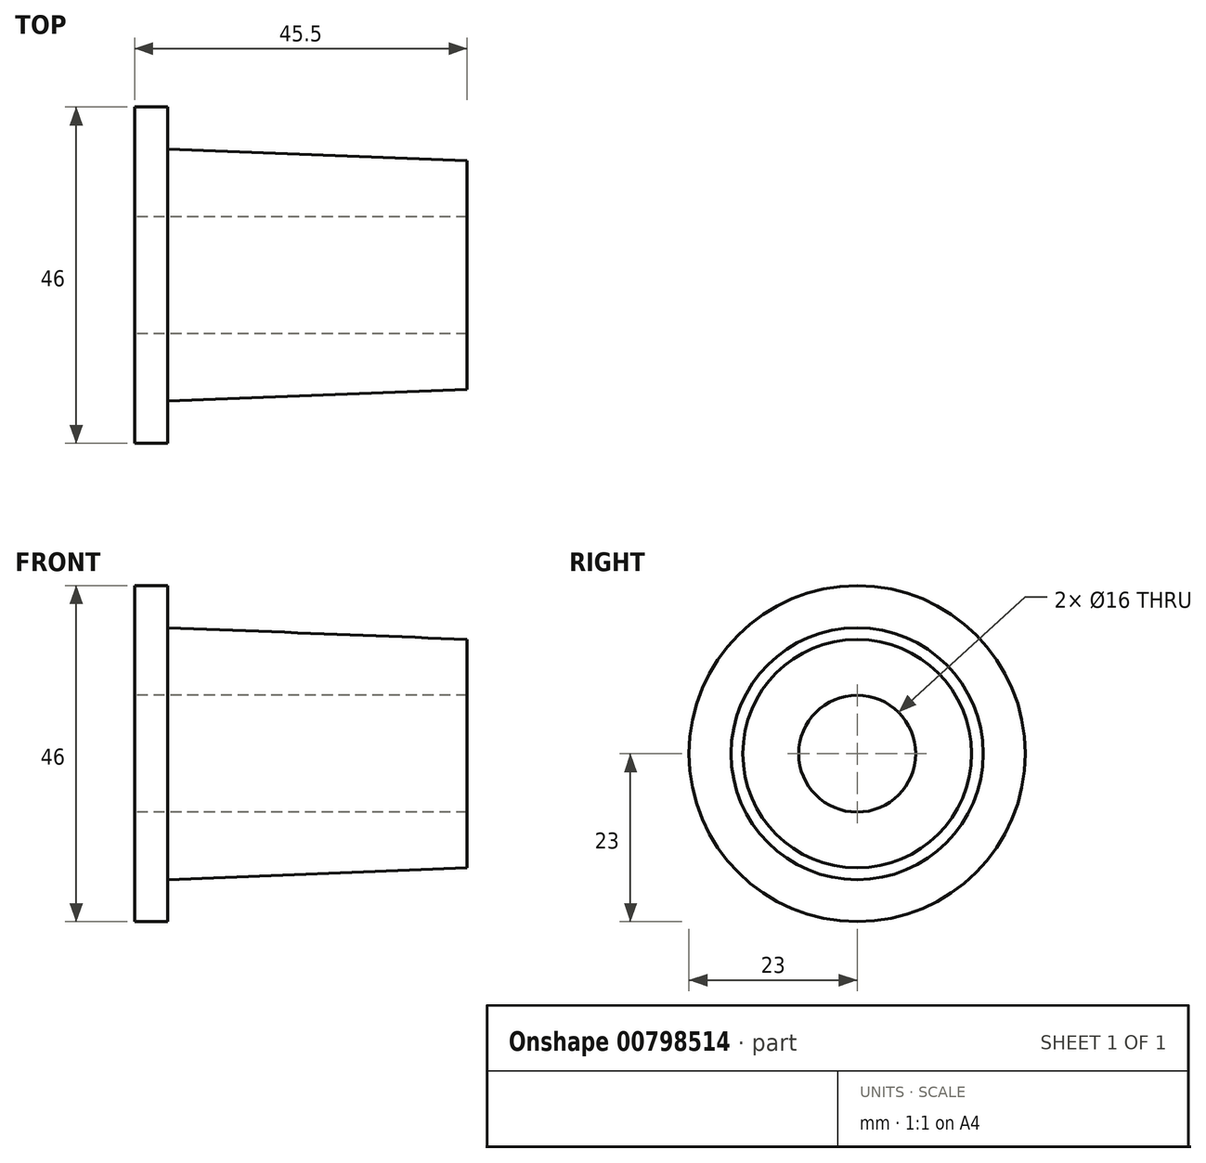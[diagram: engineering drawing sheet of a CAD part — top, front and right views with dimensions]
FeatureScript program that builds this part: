
annotation { "Feature Type Name" : "Feature", "Feature Type Description" : "" }
export const myFeature = defineFeature(function(context is Context, id is Id, definition is map)
    precondition{}
    {
        {
            var Q0;
            Q0=qCreatedBy(makeId("Front.planeOp"),FACE);
            var sketch = newSketch(context, id + "F0", { "sketchPlane" : qUnion([Q0])});
            skLineSegment(sketch, "E0", {"start": v(-62.85, 0) * mm, "end": v(69.9, 0) * mm, "construction": true});
            skLineSegment(sketch, "E1.bottom", {"start": v(0, 8) * mm, "end": v(4.5, 8) * mm});
            skLineSegment(sketch, "E1.top", {"start": v(0, 23) * mm, "end": v(4.5, 23) * mm});
            skLineSegment(sketch, "E1.left", {"start": v(0, 8) * mm, "end": v(0, 23) * mm});
            skLineSegment(sketch, "E1.right", {"start": v(4.5, 8) * mm, "end": v(4.5, 23) * mm});
            skLineSegment(sketch, "E2", {"start": v(4.5, 17.25) * mm, "end": v(45.5, 15.64) * mm});
            skLineSegment(sketch, "E3", {"start": v(45.5, 15.64) * mm, "end": v(45.5, 8) * mm});
            skLineSegment(sketch, "E4", {"start": v(45.5, 8) * mm, "end": v(4.5, 8) * mm});
            skLineSegment(sketch, "E5.MirrorCS", {"start": v(0, -8) * mm, "end": v(4.5, -8) * mm});
            skLineSegment(sketch, "E6.MirrorCS", {"start": v(0, -23) * mm, "end": v(4.5, -23) * mm});
            skLineSegment(sketch, "E7.MirrorCS", {"start": v(0, -8) * mm, "end": v(0, -23) * mm});
            skLineSegment(sketch, "E8.MirrorCS", {"start": v(45.5, -8) * mm, "end": v(4.5, -8) * mm});
            skLineSegment(sketch, "E9.MirrorCS", {"start": v(45.5, -15.64) * mm, "end": v(45.5, -8) * mm});
            skLineSegment(sketch, "E10.MirrorCS", {"start": v(4.5, -8) * mm, "end": v(4.5, -23) * mm});
            skLineSegment(sketch, "E11.MirrorCS", {"start": v(4.5, -17.25) * mm, "end": v(45.5, -15.64) * mm});
            skSolve(sketch);
        }
        {
            var Q0;
            Q0 = qSketchRegion(id + "F0", true);
            var Q1;
            Q1=sQuery(id+"F0.wireOp",EDGE,"E0");
            revolve(context, id + "F1", {"surfaceOperationType" : NewSurfaceOperationType.NEW, "entities" : qUnion([Q0]), "axis" : qUnion([Q1]), "revolveType" : RevolveType.FULL});
        }
    });
